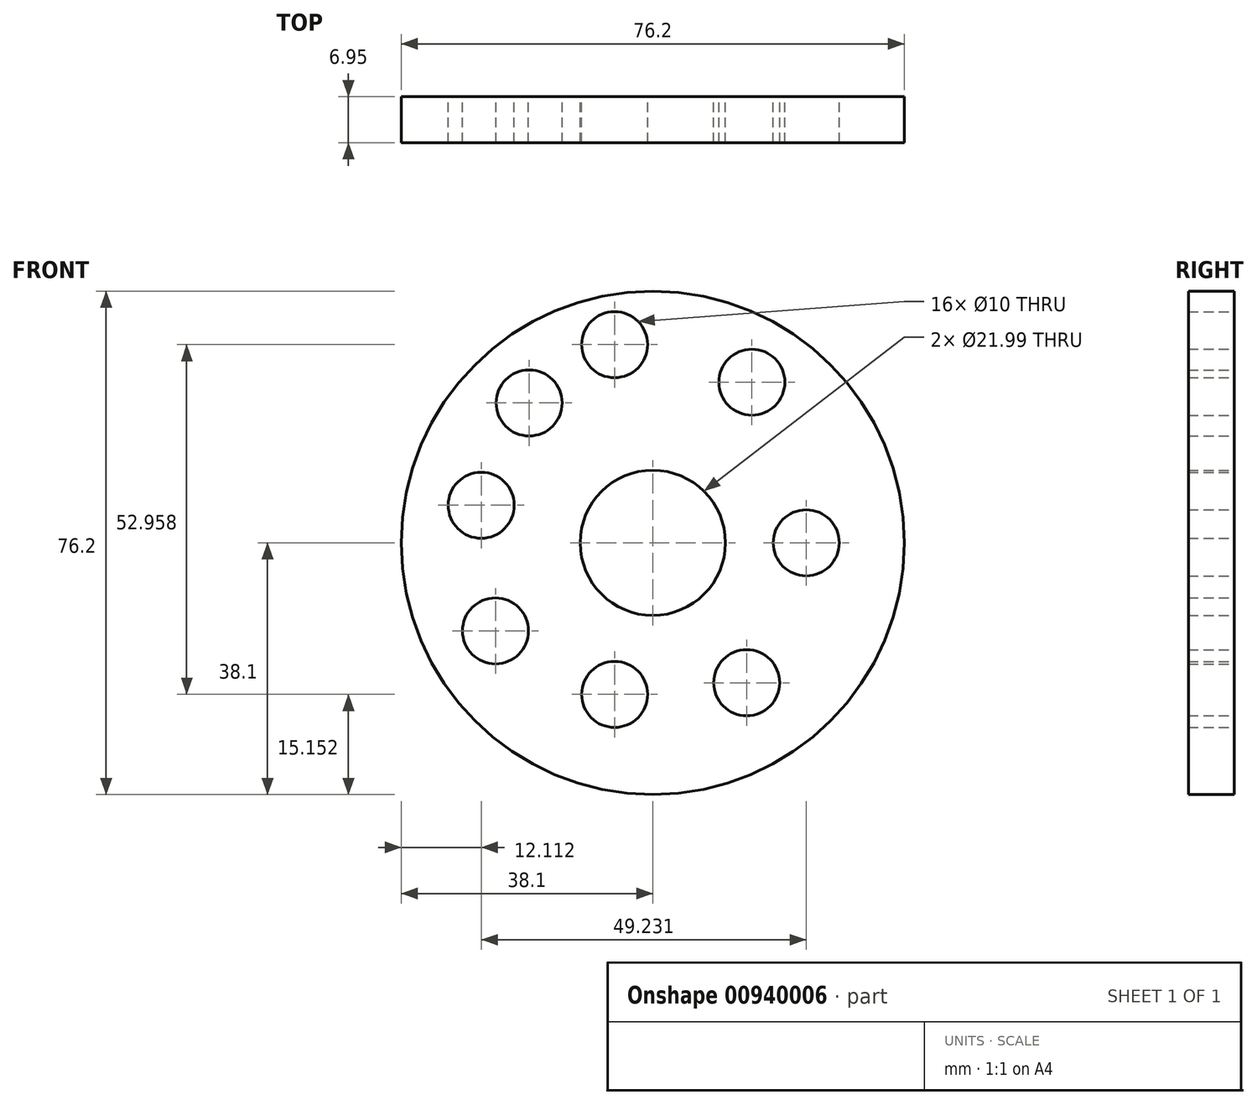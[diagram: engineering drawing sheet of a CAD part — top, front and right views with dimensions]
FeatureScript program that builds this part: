
annotation { "Feature Type Name" : "Feature", "Feature Type Description" : "" }
export const myFeature = defineFeature(function(context is Context, id is Id, definition is map)
    precondition{}
    {
        {
            var Q0;
            Q0=qCreatedBy(makeId("Front.planeOp"),FACE);
            var sketch = newSketch(context, id + "F0", { "sketchPlane" : qUnion([Q0])});
            skCircle(sketch, "E0", {"center": v(0, 0) * mm, "radius": 38.1 * mm});
            skCircle(sketch, "E1", {"center": v(-18.73, 21.18) * mm, "radius": 5 * mm});
            skCircle(sketch, "E2", {"center": v(-25.99, 5.69) * mm, "radius": 5 * mm});
            skCircle(sketch, "E3", {"center": v(-23.83, -13.34) * mm, "radius": 5 * mm});
            skCircle(sketch, "E4", {"center": v(-5.79, -22.95) * mm, "radius": 5 * mm});
            skCircle(sketch, "E5", {"center": v(14.22, -21.18) * mm, "radius": 5 * mm});
            skCircle(sketch, "E6", {"center": v(23.24, 0) * mm, "radius": 5 * mm});
            skCircle(sketch, "E7", {"center": v(15, 24.32) * mm, "radius": 5 * mm});
            skCircle(sketch, "E8", {"center": v(-5.79, 30) * mm, "radius": 5 * mm});
            skCircle(sketch, "E9", {"center": v(0, 0) * mm, "radius": 11 * mm});
            skSolve(sketch);
        }
        {
            var Q0;
            Q0=makeQuery(id+"F0.imprint","IMPRINT",FACE,{"disambiguationData":[TD([[makeQuery(id+"F0.imprint","IMPRINT",EDGE,{"derivedFrom":sQuery(id+"F0.wireOp",EDGE,"E0")}),1.0]])]});
            extrude(context, id + "F1", {"entities" : qUnion([Q0]), "depth" : 6.95 * mm, "offsetDistance" : 25 * mm});
        }
    });
